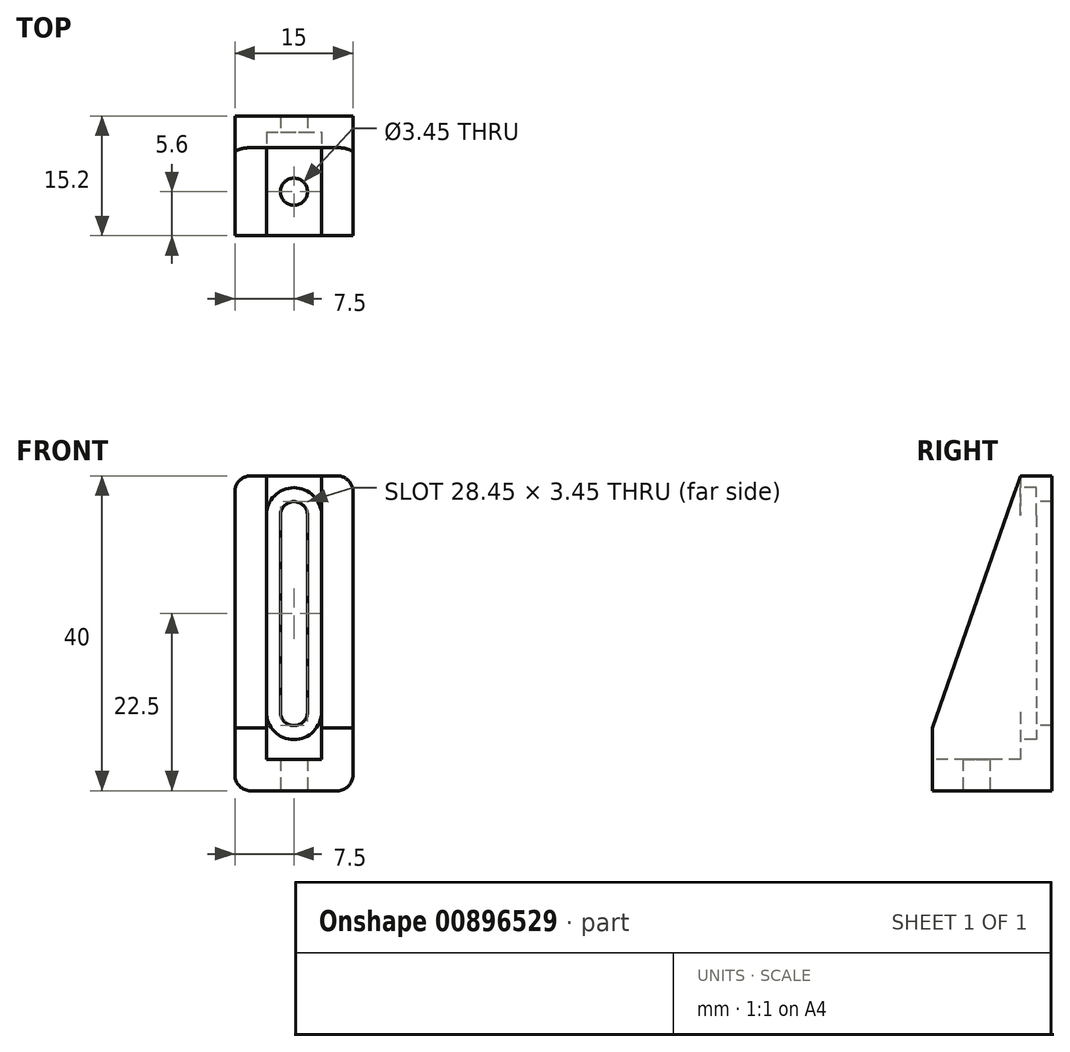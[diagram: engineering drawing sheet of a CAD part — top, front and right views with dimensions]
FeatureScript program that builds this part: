
annotation { "Feature Type Name" : "Feature", "Feature Type Description" : "" }
export const myFeature = defineFeature(function(context is Context, id is Id, definition is map)
    precondition{}
    {
        {
            var Q0;
            Q0=qCreatedBy(makeId("Top.planeOp"),FACE);
            var sketch = newSketch(context, id + "F0", { "sketchPlane" : qUnion([Q0])});
            skLineSegment(sketch, "E0.bottom", {"start": v(7.5, 7.6) * mm, "end": v(-7.5, 7.6) * mm});
            skLineSegment(sketch, "E0.top", {"start": v(7.5, -7.6) * mm, "end": v(-7.5, -7.6) * mm});
            skLineSegment(sketch, "E0.left", {"start": v(7.5, 7.6) * mm, "end": v(7.5, -7.6) * mm});
            skLineSegment(sketch, "E0.right", {"start": v(-7.5, 7.6) * mm, "end": v(-7.5, -7.6) * mm});
            skPoint(sketch, "E0.middle", {"position": v(0, 0) * mm});
            skCircle(sketch, "E1", {"center": v(0, -2) * mm, "radius": 1.73 * mm});
            skLineSegment(sketch, "E2", {"start": v(0, -2) * mm, "end": v(0, -7.6) * mm, "construction": true});
            skSolve(sketch);
        }
        {
            var Q0;
            Q0 = qSketchRegion(id + "F0", true);
            extrude(context, id + "F1", {"entities" : qUnion([Q0]), "depth" : 4 * mm, "offsetDistance" : 25 * mm});
        }
        {
            var Q0;
            Q0=makeQuery(id+"F1.opExtrude","CAP_FACE",FACE,{"disambiguationData":[OSD([sQuery(id+"F0.wireOp",EDGE,"E0.bottom"),sQuery(id+"F0.wireOp",EDGE,"E0.top"),sQuery(id+"F0.wireOp",EDGE,"E0.left"),sQuery(id+"F0.wireOp",EDGE,"E0.right"),sQuery(id+"F0.wireOp",EDGE,"E1")])],"isStart":false});
            var sketch = newSketch(context, id + "F2", { "sketchPlane" : qUnion([Q0])});
            skLineSegment(sketch, "E3", {"start": v(-7.5, -7.6) * mm, "end": v(-3.5, -7.6) * mm});
            skLineSegment(sketch, "E4", {"start": v(-3.5, -7.6) * mm, "end": v(-3.5, 3.6) * mm});
            skLineSegment(sketch, "E5", {"start": v(-3.5, 3.6) * mm, "end": v(3.5, 3.6) * mm});
            skLineSegment(sketch, "E6", {"start": v(3.5, 3.6) * mm, "end": v(3.5, -7.6) * mm});
            skLineSegment(sketch, "E7", {"start": v(3.5, -7.6) * mm, "end": v(7.5, -7.6) * mm});
            skLineSegment(sketch, "E8", {"start": v(7.5, -7.6) * mm, "end": v(7.5, 7.6) * mm});
            skLineSegment(sketch, "E9", {"start": v(7.5, 7.6) * mm, "end": v(-7.5, 7.6) * mm});
            skLineSegment(sketch, "E10", {"start": v(-7.5, 7.6) * mm, "end": v(-7.5, -7.6) * mm});
            skCircle(sketch, "E11", {"center": v(0, -2) * mm, "radius": 3.5 * mm});
            skSolve(sketch);
        }
        {
            var Q0;
            {var subQ4=sQuery(id+"F2.wireOp",EDGE,"E3");Q0=makeQuery(id+"F2.imprint","IMPRINT",FACE,{"disambiguationData":[TD([[makeQuery(id+"F2.imprint","IMPRINT",EDGE,{"derivedFrom":subQ4}),-1.0]])]});}
            extrude(context, id + "F3", {"entities" : qUnion([Q0]), "operationType" : NewBodyOperationType.ADD, "depth" : 36 * mm, "offsetDistance" : 25 * mm});
        }
        {
            var Q0;
            Q0=makeQuery(id+"F3.opExtrude","SWEPT_FACE",FACE,{"disambiguationData":[OSD([sQuery(id+"F2.wireOp",EDGE,"E5")])]});
            var sketch = newSketch(context, id + "F4", { "sketchPlane" : qUnion([Q0])});
            skLineSegment(sketch, "E12", {"start": v(0, 0) * mm, "end": v(0, 35) * mm, "construction": true});
            skCircle(sketch, "E13", {"center": v(0, 35) * mm, "radius": 1.73 * mm});
            skCircle(sketch, "E14", {"center": v(0, 35) * mm, "radius": 3.5 * mm});
            skCircle(sketch, "E15", {"center": v(0, 10) * mm, "radius": 1.73 * mm});
            skCircle(sketch, "E16", {"center": v(0, 10) * mm, "radius": 3.5 * mm});
            skLineSegment(sketch, "E17", {"start": v(-1.73, 10) * mm, "end": v(-1.73, 35) * mm});
            skLineSegment(sketch, "E18", {"start": v(1.73, 35) * mm, "end": v(1.73, 10) * mm});
            skSolve(sketch);
        }
        {
            var Q0;
            {var subQ0=sQuery(id+"F4.wireOp",EDGE,"E17");var subQ1=sQuery(id+"F4.wireOp",EDGE,"E14");var subQ2=makeQuery(id+"F4.imprint","INTERSECT",VERTEX,{"derivedFrom":[subQ1,subQ0]});Q0=makeQuery(id+"F4.imprint","IMPRINT",FACE,{"disambiguationData":[TD([[makeQuery(id+"F4.imprint","IMPRINT",EDGE,{"disambiguationData":[TD([[subQ2,1.0]])],"derivedFrom":subQ0}),1.0]])]});}
            var Q1;
            {var subQ0=sQuery(id+"F4.wireOp",EDGE,"E18");var subQ1=sQuery(id+"F4.wireOp",EDGE,"E14");var subQ2=makeQuery(id+"F4.imprint","INTERSECT",VERTEX,{"derivedFrom":[subQ1,subQ0]});Q1=makeQuery(id+"F4.imprint","IMPRINT",FACE,{"disambiguationData":[TD([[makeQuery(id+"F4.imprint","IMPRINT",EDGE,{"disambiguationData":[TD([[subQ2,-1.0]])],"derivedFrom":subQ0}),1.0]])]});}
            var Q2;
            {var subQ0=sQuery(id+"F4.wireOp",EDGE,"E17");var subQ5=sQuery(id+"F4.wireOp",EDGE,"E13");var subQ6=makeQuery(id+"F4.imprint","INTERSECT",VERTEX,{"derivedFrom":[subQ5,subQ0]});Q2=makeQuery(id+"F4.imprint","IMPRINT",FACE,{"disambiguationData":[TD([[makeQuery(id+"F4.imprint","IMPRINT",EDGE,{"disambiguationData":[TD([[subQ6,1.0]])],"derivedFrom":subQ5}),-1.0]])]});}
            var Q3;
            {var subQ4=sQuery(id+"F4.wireOp",EDGE,"E17");var subQ8=sQuery(id+"F4.wireOp",EDGE,"E15");var subQ9=makeQuery(id+"F4.imprint","INTERSECT",VERTEX,{"derivedFrom":[subQ8,subQ4]});Q3=makeQuery(id+"F4.imprint","IMPRINT",FACE,{"disambiguationData":[TD([[makeQuery(id+"F4.imprint","IMPRINT",EDGE,{"disambiguationData":[TD([[subQ9,-1.0]])],"derivedFrom":subQ8}),-1.0]])]});}
            extrude(context, id + "F5", {"entities" : qUnion([Q0, Q1, Q2, Q3]), "operationType" : NewBodyOperationType.REMOVE, "oppositeDirection" : true, "depth" : 2 * mm, "offsetDistance" : 25 * mm});
        }
        {
            var Q0;
            Q0=makeQuery(id+"F4.imprint","IMPRINT",FACE,{"disambiguationData":[TD([[makeQuery(id+"F4.imprint","IMPRINT",EDGE,{"derivedFrom":sQuery(id+"F4.wireOp",EDGE,"E13")}),1.0]])]});
            var Q1;
            {var subQ0=sQuery(id+"F4.wireOp",EDGE,"E17");var subQ1=sQuery(id+"F4.wireOp",EDGE,"E13");var subQ2=makeQuery(id+"F4.imprint","INTERSECT",VERTEX,{"derivedFrom":[subQ1,subQ0]});Q1=makeQuery(id+"F4.imprint","IMPRINT",FACE,{"disambiguationData":[TD([[makeQuery(id+"F4.imprint","IMPRINT",EDGE,{"disambiguationData":[TD([[subQ2,-1.0]])],"derivedFrom":subQ1}),-1.0]])]});}
            var Q2;
            {var subQ0=sQuery(id+"F4.wireOp",EDGE,"E17");var subQ1=sQuery(id+"F4.wireOp",EDGE,"E14");var subQ2=makeQuery(id+"F4.imprint","INTERSECT",VERTEX,{"derivedFrom":[subQ1,subQ0]});Q2=makeQuery(id+"F4.imprint","IMPRINT",FACE,{"disambiguationData":[TD([[makeQuery(id+"F4.imprint","IMPRINT",EDGE,{"disambiguationData":[TD([[subQ2,-1.0]])],"derivedFrom":subQ1}),-1.0]])]});}
            var Q3;
            {var subQ0=sQuery(id+"F4.wireOp",EDGE,"E17");var subQ1=sQuery(id+"F4.wireOp",EDGE,"E15");var subQ2=makeQuery(id+"F4.imprint","INTERSECT",VERTEX,{"derivedFrom":[subQ1,subQ0]});Q3=makeQuery(id+"F4.imprint","IMPRINT",FACE,{"disambiguationData":[TD([[makeQuery(id+"F4.imprint","IMPRINT",EDGE,{"disambiguationData":[TD([[subQ2,1.0]])],"derivedFrom":subQ1}),-1.0]])]});}
            var Q4;
            {var subQ0=sQuery(id+"F4.wireOp",EDGE,"E15");var subQ1=makeQuery(id+"F4.imprint","INTERSECT",VERTEX,{"derivedFrom":[subQ0,sQuery(id+"F4.wireOp",EDGE,"E17")]});Q4=makeQuery(id+"F4.imprint","IMPRINT",FACE,{"disambiguationData":[TD([[makeQuery(id+"F4.imprint","IMPRINT",EDGE,{"disambiguationData":[TD([[subQ1,1.0]])],"derivedFrom":subQ0}),1.0]])]});}
            extrude(context, id + "F6", {"entities" : qUnion([Q0, Q1, Q2, Q3, Q4]), "operationType" : NewBodyOperationType.REMOVE, "endBound" : BoundingType.UP_TO_NEXT, "oppositeDirection" : true, "depth" : 25 * mm, "offsetDistance" : 25 * mm});
        }
        {
            var Q0;
            Q0=makeQuery(id+"F3.opExtrude","CAP_EDGE",EDGE,{"disambiguationData":[OSD([sQuery(id+"F2.wireOp",EDGE,"E7")])],"isStart":false});
            var Q1;
            Q1=makeQuery(id+"F3.opExtrude","CAP_EDGE",EDGE,{"disambiguationData":[OSD([sQuery(id+"F2.wireOp",EDGE,"E3")])],"isStart":false});
            chamfer(context, id + "F7", {"entities" : qUnion([Q0, Q1]), "chamferType" : ChamferType.TWO_OFFSETS, "width1" : 32 * mm, "oppositeDirection" : false, "width2" : 11.2 * mm, "tangentPropagation" : true});
        }
        {
            var Q0;
            Q0=makeQuery(id+"F3.opExtrude","CAP_EDGE",EDGE,{"disambiguationData":[OSD([sQuery(id+"F2.wireOp",EDGE,"E10")])],"isStart":false});
            var Q1;
            Q1=makeQuery(id+"F3.opExtrude","CAP_EDGE",EDGE,{"disambiguationData":[OSD([sQuery(id+"F2.wireOp",EDGE,"E8")])],"isStart":false});
            var Q2;
            Q2=makeQuery(id+"F1.opExtrude","CAP_EDGE",EDGE,{"disambiguationData":[OSD([sQuery(id+"F0.wireOp",EDGE,"E0.right")])],"isStart":true});
            var Q3;
            Q3=makeQuery(id+"F1.opExtrude","CAP_EDGE",EDGE,{"disambiguationData":[OSD([sQuery(id+"F0.wireOp",EDGE,"E0.left")])],"isStart":true});
            fillet(context, id + "F8", {"entities" : qUnion([Q0, Q1, Q2, Q3]), "tangentPropagation" : true, "radius" : 2 * mm, "defaultsChanged" : true, "vertexSettings" : [], "allowEdgeOverflow" : false});
        }
    });
